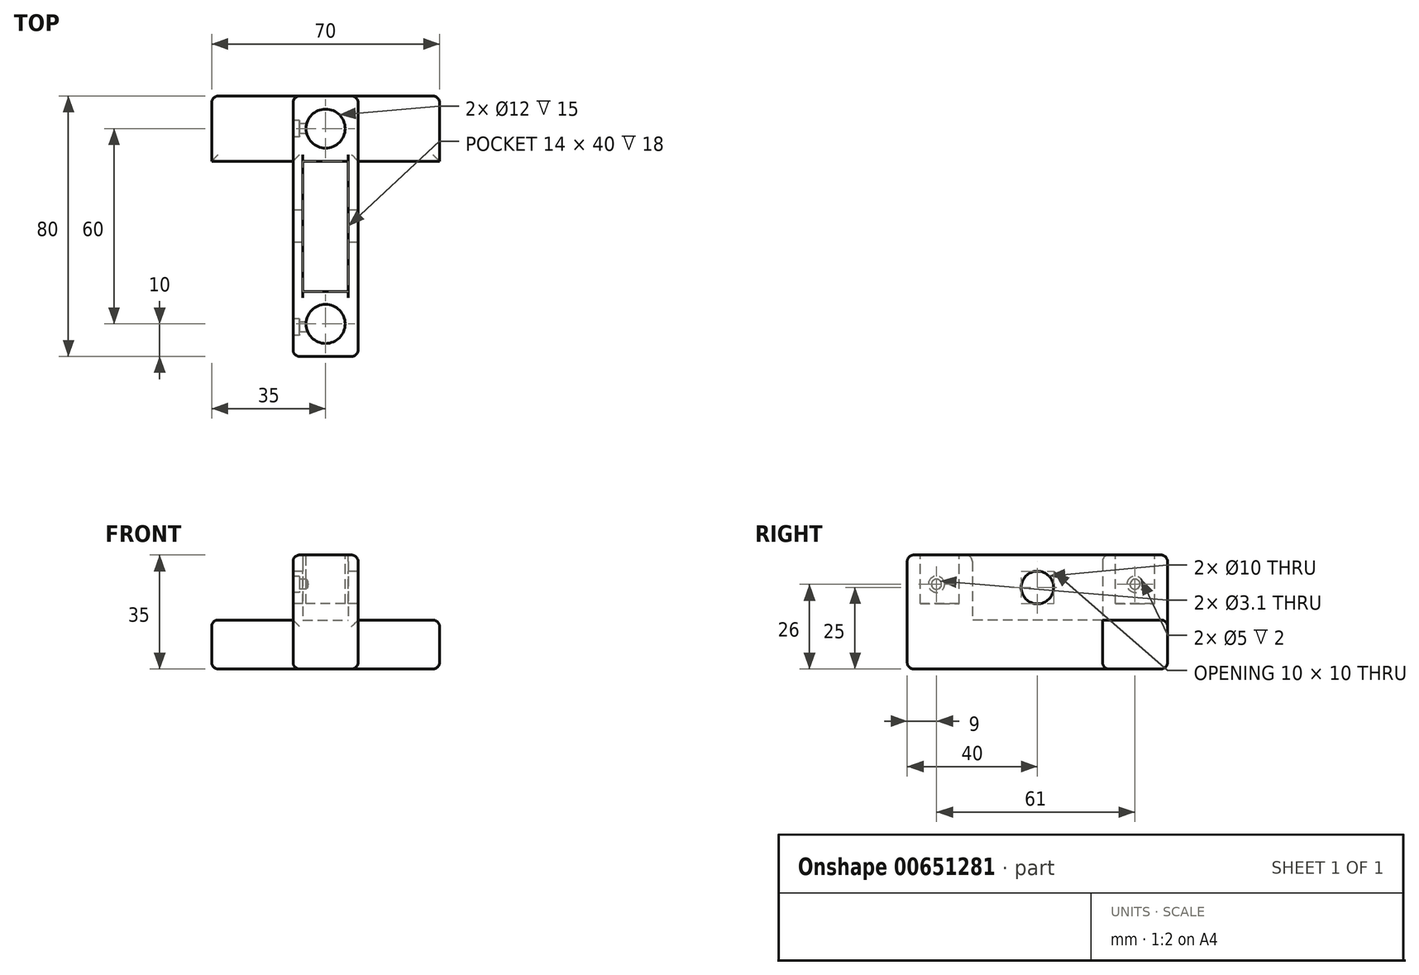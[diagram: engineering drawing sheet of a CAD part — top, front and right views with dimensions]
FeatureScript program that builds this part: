
annotation { "Feature Type Name" : "Feature", "Feature Type Description" : "" }
export const myFeature = defineFeature(function(context is Context, id is Id, definition is map)
    precondition{}
    {
        {
            var Q0;
            Q0=qCreatedBy(makeId("Top.planeOp"),FACE);
            var sketch = newSketch(context, id + "F0", { "sketchPlane" : qUnion([Q0])});
            skLineSegment(sketch, "E0", {"start": v(0, 0) * mm, "end": v(0, 60) * mm});
            skLineSegment(sketch, "E1", {"start": v(-20, 60) * mm, "end": v(-20, 0) * mm});
            skLineSegment(sketch, "E2", {"start": v(-20, 0) * mm, "end": v(0, 0) * mm});
            skLineSegment(sketch, "E3", {"start": v(-20, 60) * mm, "end": v(-45, 60) * mm});
            skLineSegment(sketch, "E4", {"start": v(0, 60) * mm, "end": v(25, 60) * mm});
            skLineSegment(sketch, "E5", {"start": v(25, 60) * mm, "end": v(25, 80) * mm});
            skLineSegment(sketch, "E6", {"start": v(25, 80) * mm, "end": v(-45, 80) * mm});
            skLineSegment(sketch, "E7", {"start": v(-45, 60) * mm, "end": v(-45, 80) * mm});
            skSolve(sketch);
        }
        {
            var Q0;
            Q0=qSketchRegion(id+"F0",true);
            extrude(context, id + "F1", {"entities" : qUnion([Q0]), "depth" : 15 * mm, "offsetDistance" : 25 * mm});
        }
        {
            var Q0;
            Q0=makeQuery(id+"F1.opExtrude","CAP_FACE",FACE,{"disambiguationData":[OSD([sQuery(id+"F0.wireOp",EDGE,"E0"),sQuery(id+"F0.wireOp",EDGE,"IpwEPH2j-ZLUt-4eao-T1zL-93qLtNCBv986"),sQuery(id+"F0.wireOp",EDGE,"IkMCroVT-TcKO-eUqF-MIY3-maLz9PJaoaBo"),sQuery(id+"F0.wireOp",EDGE,"Y71NGfBd-OmAl-usyz-xlyV-XkMFEVhfQpSt"),sQuery(id+"F0.wireOp",EDGE,"E1"),sQuery(id+"F0.wireOp",EDGE,"E2")])],"isStart":false});
            var sketch = newSketch(context, id + "F2", { "sketchPlane" : qUnion([Q0])});
            skLineSegment(sketch, "E8", {"start": v(0, 0) * mm, "end": v(-20, 0) * mm});
            skLineSegment(sketch, "E9", {"start": v(-20, 0) * mm, "end": v(-20, 20) * mm});
            skLineSegment(sketch, "E10", {"start": v(-20, 20) * mm, "end": v(0, 20) * mm});
            skLineSegment(sketch, "E11", {"start": v(0, 20) * mm, "end": v(0, 0) * mm});
            skSolve(sketch);
        }
        {
            var Q0;
            Q0 = qSketchRegion(id + "F2", true);
            var Q1;
            {var subQ0=sQuery(id+"F2.wireOp",EDGE,"E8");Q1=makeQuery(id+"F2.imprint","IMPRINT",FACE,{"disambiguationData":[TD([[makeQuery(id+"F2.imprint","IMPRINT",EDGE,{"derivedFrom":subQ0}),1.0]])]});}
            extrude(context, id + "F3", {"entities" : qUnion([Q0, Q1]), "operationType" : NewBodyOperationType.ADD, "depth" : 20 * mm, "offsetDistance" : 25 * mm});
        }
        {
            var Q0;
            Q0=makeQuery(id+"F3.opExtrude","CAP_FACE",FACE,{"disambiguationData":[OSD([sQuery(id+"F2.wireOp",EDGE,"E9"),sQuery(id+"F2.wireOp",EDGE,"E10"),sQuery(id+"F2.wireOp",EDGE,"E11"),sQuery(id+"F2.wireOp",EDGE,"E8")])],"isStart":false});
            var sketch = newSketch(context, id + "F4", { "sketchPlane" : qUnion([Q0])});
            skLineSegment(sketch, "E12", {"start": v(-20, 0) * mm, "end": v(-10, 0) * mm});
            skLineSegment(sketch, "E13", {"start": v(-10, 0) * mm, "end": v(-10, 10) * mm});
            skCircle(sketch, "E14", {"center": v(-10, 10) * mm, "radius": 6 * mm});
            skSolve(sketch);
        }
        {
            var Q0;
            Q0 = qSketchRegion(id + "F4", true);
            extrude(context, id + "F5", {"entities" : qUnion([Q0]), "operationType" : NewBodyOperationType.REMOVE, "oppositeDirection" : true, "depth" : 15 * mm, "offsetDistance" : 25 * mm});
        }
        {
            var Q0;
            Q0=makeQuery(id+"F1.opExtrude","CAP_FACE",FACE,{"disambiguationData":[OSD([sQuery(id+"F0.wireOp",EDGE,"E0"),sQuery(id+"F0.wireOp",EDGE,"E1"),sQuery(id+"F0.wireOp",EDGE,"E2"),sQuery(id+"F0.wireOp",EDGE,"E3"),sQuery(id+"F0.wireOp",EDGE,"E4"),sQuery(id+"F0.wireOp",EDGE,"E5"),sQuery(id+"F0.wireOp",EDGE,"E6"),sQuery(id+"F0.wireOp",EDGE,"E7")])],"isStart":false});
            var sketch = newSketch(context, id + "F6", { "sketchPlane" : qUnion([Q0])});
            skPoint(sketch, "E15.endSnap0", {"position": v(-10, 20) * mm});
            skLineSegment(sketch, "E16", {"start": v(-20, 60) * mm, "end": v(0, 60) * mm});
            skLineSegment(sketch, "E17", {"start": v(0, 60) * mm, "end": v(0, 80) * mm});
            skPoint(sketch, "E15.end.orphan", {"position": v(-10, 70) * mm});
            skPoint(sketch, "E18.end.orphan", {"position": v(-10, 80) * mm});
            skLineSegment(sketch, "E19", {"start": v(-20, 60) * mm, "end": v(-20, 80) * mm});
            skLineSegment(sketch, "E20", {"start": v(-20, 80) * mm, "end": v(0, 80) * mm});
            skSolve(sketch);
        }
        {
            var Q0;
            Q0 = qSketchRegion(id + "F6", true);
            extrude(context, id + "F7", {"entities" : qUnion([Q0]), "operationType" : NewBodyOperationType.ADD, "depth" : 20 * mm, "offsetDistance" : 25 * mm});
        }
        {
            var Q0;
            Q0=makeQuery(id+"F7.opExtrude","CAP_FACE",FACE,{"disambiguationData":[OSD([sQuery(id+"F6.wireOp",EDGE,"E16"),sQuery(id+"F6.wireOp",EDGE,"E17"),sQuery(id+"F6.wireOp",EDGE,"E19"),sQuery(id+"F6.wireOp",EDGE,"E20")])],"isStart":false});
            var sketch = newSketch(context, id + "F8", { "sketchPlane" : qUnion([Q0])});
            skLineSegment(sketch, "E21", {"start": v(-20, 60) * mm, "end": v(-10, 60) * mm});
            skLineSegment(sketch, "E22", {"start": v(-10, 60) * mm, "end": v(-10, 70) * mm});
            skCircle(sketch, "E23", {"center": v(-10, 70) * mm, "radius": 6 * mm});
            skSolve(sketch);
        }
        {
            var Q0;
            Q0 = qSketchRegion(id + "F8", true);
            extrude(context, id + "F9", {"entities" : qUnion([Q0]), "operationType" : NewBodyOperationType.REMOVE, "oppositeDirection" : true, "depth" : 15 * mm, "offsetDistance" : 25 * mm});
        }
        {
            var Q0;
            {var subQ0=sQuery(id+"F0.wireOp",EDGE,"E4");var subQ1=sQuery(id+"F0.wireOp",EDGE,"E0");var subQ2=sQuery(id+"F0.wireOp",EDGE,"E3");var subQ3=sQuery(id+"F0.wireOp",EDGE,"E1");var subQ4=makeQuery(id+"F1.opExtrude","CAP_FACE",FACE,{"disambiguationData":[OSD([subQ1,subQ3,sQuery(id+"F0.wireOp",EDGE,"E2"),subQ2,subQ0,sQuery(id+"F0.wireOp",EDGE,"E5"),sQuery(id+"F0.wireOp",EDGE,"E6"),sQuery(id+"F0.wireOp",EDGE,"E7")])],"isStart":false});Q0=makeQuery(id+"F7.boolean.opBoolean","SPLIT",FACE,{"disambiguationData":[TD([makeQuery(id+"F3.opExtrude","SWEPT_FACE",FACE,{"disambiguationData":[OSD([sQuery(id+"F2.wireOp",EDGE,"E10")])]})])],"derivedFrom":subQ4});}
            var sketch = newSketch(context, id + "F10", { "sketchPlane" : qUnion([Q0])});
            skLineSegment(sketch, "E24", {"start": v(0, 20) * mm, "end": v(0, 60) * mm});
            skLineSegment(sketch, "E25", {"start": v(0, 60) * mm, "end": v(-3, 60) * mm});
            skLineSegment(sketch, "E26", {"start": v(-3, 60) * mm, "end": v(-3, 20) * mm});
            skLineSegment(sketch, "E27", {"start": v(0, 20) * mm, "end": v(-3, 20) * mm});
            skLineSegment(sketch, "E28", {"start": v(-20, 20) * mm, "end": v(-20, 60) * mm});
            skLineSegment(sketch, "E29", {"start": v(-20, 60) * mm, "end": v(-17, 60) * mm});
            skLineSegment(sketch, "E30", {"start": v(-17, 60) * mm, "end": v(-17, 20) * mm});
            skLineSegment(sketch, "E31", {"start": v(-17, 20) * mm, "end": v(-20, 20) * mm});
            skSolve(sketch);
        }
        {
            var Q0;
            Q0 = qSketchRegion(id + "F10", true);
            extrude(context, id + "F11", {"entities" : qUnion([Q0]), "operationType" : NewBodyOperationType.ADD, "depth" : 20 * mm, "offsetDistance" : 25 * mm});
        }
        {
            var Q0;
            Q0=makeQuery(id+"F11.boolean.opBoolean","MERGE",FACE,{"derivedFrom":[makeQuery(id+"F3.boolean.opBoolean","MERGE",FACE,{"derivedFrom":[makeQuery(id+"F1.opExtrude","SWEPT_FACE",FACE,{"disambiguationData":[OSD([sQuery(id+"F0.wireOp",EDGE,"E1")])]}),makeQuery(id+"F3.opExtrude","SWEPT_FACE",FACE,{"disambiguationData":[OSD([sQuery(id+"F2.wireOp",EDGE,"E9")])]})]}),makeQuery(id+"F7.opExtrude","SWEPT_FACE",FACE,{"disambiguationData":[OSD([sQuery(id+"F6.wireOp",EDGE,"E19")])]}),makeQuery(id+"F11.opExtrude","SWEPT_FACE",FACE,{"disambiguationData":[OSD([sQuery(id+"F10.wireOp",EDGE,"E28")])]})]});
            var sketch = newSketch(context, id + "F12", { "sketchPlane" : qUnion([Q0])});
            skLineSegment(sketch, "E32", {"start": v(0, 35) * mm, "end": v(0, 25) * mm});
            skLineSegment(sketch, "E33", {"start": v(0, 25) * mm, "end": v(-40, 25) * mm});
            skCircle(sketch, "E34", {"center": v(-40, 25) * mm, "radius": 5 * mm});
            skSolve(sketch);
        }
        {
            var Q0;
            Q0 = qSketchRegion(id + "F12", true);
            extrude(context, id + "F13", {"entities" : qUnion([Q0]), "operationType" : NewBodyOperationType.REMOVE, "oppositeDirection" : true, "depth" : 25 * mm, "offsetDistance" : 25 * mm});
        }
        {
            var Q0;
            Q0=makeQuery(id+"F11.boolean.opBoolean","MERGE",EDGE,{"derivedFrom":[makeQuery(id+"F3.opExtrude","CAP_EDGE",EDGE,{"disambiguationData":[OSD([sQuery(id+"F2.wireOp",EDGE,"E9")])],"isStart":false}),makeQuery(id+"F7.opExtrude","CAP_EDGE",EDGE,{"disambiguationData":[OSD([sQuery(id+"F6.wireOp",EDGE,"E19")])],"isStart":false}),makeQuery(id+"F11.opExtrude","CAP_EDGE",EDGE,{"disambiguationData":[OSD([sQuery(id+"F10.wireOp",EDGE,"E28")])],"isStart":false})]});
            var Q1;
            Q1=makeQuery(id+"F11.boolean.opBoolean","MERGE",EDGE,{"derivedFrom":[makeQuery(id+"F3.opExtrude","CAP_EDGE",EDGE,{"disambiguationData":[OSD([sQuery(id+"F2.wireOp",EDGE,"E11")])],"isStart":false}),makeQuery(id+"F7.opExtrude","CAP_EDGE",EDGE,{"disambiguationData":[OSD([sQuery(id+"F6.wireOp",EDGE,"E17")])],"isStart":false}),makeQuery(id+"F11.opExtrude","CAP_EDGE",EDGE,{"disambiguationData":[OSD([sQuery(id+"F10.wireOp",EDGE,"E24")])],"isStart":false})]});
            fillet(context, id + "F14", {"entities" : qUnion([Q0, Q1]), "radius" : 2 * mm, "tangentPropagation" : true, "allowEdgeOverflow" : false});
        }
        {
            var Q0;
            Q0=makeQuery(id+"F3.opExtrude","CAP_EDGE",EDGE,{"disambiguationData":[OSD([sQuery(id+"F2.wireOp",EDGE,"E10")])],"isStart":false});
            var Q1;
            Q1=makeQuery(id+"F7.opExtrude","CAP_EDGE",EDGE,{"disambiguationData":[OSD([sQuery(id+"F6.wireOp",EDGE,"E16")])],"isStart":false});
            var Q2;
            Q2=makeQuery(id+"F7.opExtrude","CAP_EDGE",EDGE,{"disambiguationData":[OSD([sQuery(id+"F6.wireOp",EDGE,"E20")])],"isStart":false});
            var Q3;
            Q3=makeQuery(id+"F3.opExtrude","CAP_EDGE",EDGE,{"disambiguationData":[OSD([sQuery(id+"F2.wireOp",EDGE,"E8")])],"isStart":false});
            fillet(context, id + "F15", {"entities" : qUnion([Q0, Q1, Q2, Q3]), "radius" : 2 * mm, "tangentPropagation" : true, "allowEdgeOverflow" : false});
        }
        {
            var Q0;
            {var subQ0=sQuery(id+"F0.wireOp",EDGE,"E7");var subQ1=sQuery(id+"F0.wireOp",EDGE,"E6");Q0=makeQuery(id+"F7.boolean.opBoolean","SPLIT",EDGE,{"disambiguationData":[TD([makeQuery(id+"F1.opExtrude","SWEPT_FACE",FACE,{"disambiguationData":[OSD([subQ0])]})])],"derivedFrom":makeQuery(id+"F1.opExtrude","CAP_EDGE",EDGE,{"disambiguationData":[OSD([subQ1])],"isStart":false})});}
            var Q1;
            {var subQ0=sQuery(id+"F0.wireOp",EDGE,"E6");var subQ1=sQuery(id+"F0.wireOp",EDGE,"E5");Q1=makeQuery(id+"F7.boolean.opBoolean","SPLIT",EDGE,{"disambiguationData":[TD([makeQuery(id+"F1.opExtrude","SWEPT_FACE",FACE,{"disambiguationData":[OSD([subQ1])]})])],"derivedFrom":makeQuery(id+"F1.opExtrude","CAP_EDGE",EDGE,{"disambiguationData":[OSD([subQ0])],"isStart":false})});}
            fillet(context, id + "F16", {"entities" : qUnion([Q0, Q1]), "radius" : 2 * mm, "tangentPropagation" : true, "allowEdgeOverflow" : false});
        }
        {
            var Q0;
            Q0=makeQuery(id+"F1.opExtrude","CAP_EDGE",EDGE,{"disambiguationData":[OSD([sQuery(id+"F0.wireOp",EDGE,"E1")])],"isStart":true});
            var Q1;
            Q1=makeQuery(id+"F1.opExtrude","CAP_EDGE",EDGE,{"disambiguationData":[OSD([sQuery(id+"F0.wireOp",EDGE,"E3")])],"isStart":true});
            var Q2;
            Q2=makeQuery(id+"F1.opExtrude","CAP_EDGE",EDGE,{"disambiguationData":[OSD([sQuery(id+"F0.wireOp",EDGE,"E4")])],"isStart":true});
            var Q3;
            Q3=makeQuery(id+"F1.opExtrude","CAP_EDGE",EDGE,{"disambiguationData":[OSD([sQuery(id+"F0.wireOp",EDGE,"E7")])],"isStart":true});
            var Q4;
            Q4=makeQuery(id+"F1.opExtrude","CAP_EDGE",EDGE,{"disambiguationData":[OSD([sQuery(id+"F0.wireOp",EDGE,"E5")])],"isStart":true});
            var Q5;
            Q5=makeQuery(id+"F1.opExtrude","CAP_EDGE",EDGE,{"disambiguationData":[OSD([sQuery(id+"F0.wireOp",EDGE,"E6")])],"isStart":true});
            var Q6;
            Q6=makeQuery(id+"F1.opExtrude","SWEPT_EDGE",EDGE,{"disambiguationData":[OSD([sQuery(id+"F0.wireOp",EDGE,"E6"),sQuery(id+"F0.wireOp",EDGE,"E7")])]});
            var Q7;
            Q7=makeQuery(id+"F1.opExtrude","SWEPT_EDGE",EDGE,{"disambiguationData":[OSD([sQuery(id+"F0.wireOp",EDGE,"E5"),sQuery(id+"F0.wireOp",EDGE,"E6")])]});
            fillet(context, id + "F17", {"entities" : qUnion([Q0, Q1, Q2, Q3, Q4, Q5, Q6, Q7]), "radius" : 2 * mm, "tangentPropagation" : true, "allowEdgeOverflow" : false});
        }
        {
            var Q0;
            Q0=makeQuery(id+"F11.boolean.opBoolean","MERGE",FACE,{"derivedFrom":[makeQuery(id+"F3.boolean.opBoolean","MERGE",FACE,{"derivedFrom":[makeQuery(id+"F1.opExtrude","SWEPT_FACE",FACE,{"disambiguationData":[OSD([sQuery(id+"F0.wireOp",EDGE,"E1")])]}),makeQuery(id+"F3.opExtrude","SWEPT_FACE",FACE,{"disambiguationData":[OSD([sQuery(id+"F2.wireOp",EDGE,"E9")])]})]}),makeQuery(id+"F7.opExtrude","SWEPT_FACE",FACE,{"disambiguationData":[OSD([sQuery(id+"F6.wireOp",EDGE,"E19")])]}),makeQuery(id+"F11.opExtrude","SWEPT_FACE",FACE,{"disambiguationData":[OSD([sQuery(id+"F10.wireOp",EDGE,"E28")])]})]});
            var sketch = newSketch(context, id + "F18", { "sketchPlane" : qUnion([Q0])});
            skLineSegment(sketch, "E35", {"start": v(-2, 33) * mm, "end": v(-2, 26) * mm});
            skLineSegment(sketch, "E36", {"start": v(-2, 26) * mm, "end": v(-9, 26) * mm});
            skLineSegment(sketch, "E37", {"start": v(-78, 33) * mm, "end": v(-78, 26) * mm});
            skLineSegment(sketch, "E38", {"start": v(-78, 26) * mm, "end": v(-70, 26) * mm});
            skSolve(sketch);
        }
        {
            var Q0;
            Q0=sQuery(id+"F18.wireOp",VERTEX,"E38.end");
            var Q1;
            Q1=sQuery(id+"F18.wireOp",VERTEX,"E36.end");
            var Q2;
            Q2=makeQuery(id+"F1.opExtrude","SWEPT_BODY",BODY,{"disambiguationData":[OSD([sQuery(id+"F0.wireOp",EDGE,"E0"),sQuery(id+"F0.wireOp",EDGE,"E1"),sQuery(id+"F0.wireOp",EDGE,"E2"),sQuery(id+"F0.wireOp",EDGE,"E3"),sQuery(id+"F0.wireOp",EDGE,"E4"),sQuery(id+"F0.wireOp",EDGE,"E5"),sQuery(id+"F0.wireOp",EDGE,"E6"),sQuery(id+"F0.wireOp",EDGE,"E7")])]});
            hole(context, id + "F19", {"style" : HoleStyle.C_BORE, "endStyle" : HoleEndStyle.BLIND, "holeDiameter" : 3.1 * mm, "cBoreDiameter" : 5 * mm, "cBoreDepth" : 2 * mm, "majorDiameter" : 5 * mm, "holeDepth" : 6 * mm, "isTappedThrough" : true, "tappedDepth" : 12 * mm, "tapClearance" : 3, "locations" : qUnion([Q0, Q1]), "scope" : qUnion([Q2])});
        }
    });
